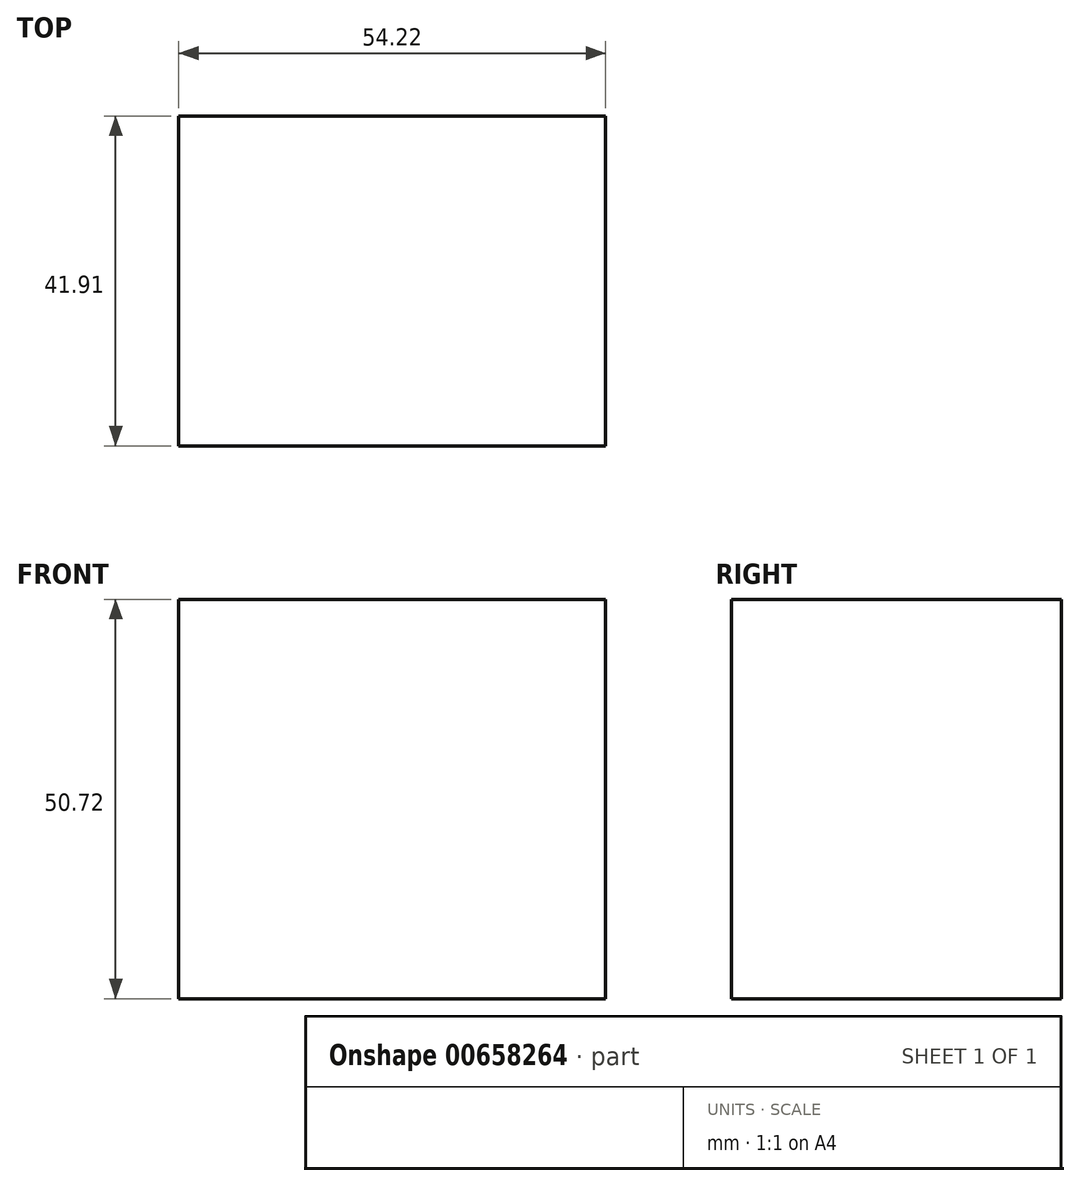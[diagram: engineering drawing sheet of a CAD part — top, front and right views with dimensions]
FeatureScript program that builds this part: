
annotation { "Feature Type Name" : "Feature", "Feature Type Description" : "" }
export const myFeature = defineFeature(function(context is Context, id is Id, definition is map)
    precondition{}
    {
        {
            var Q0;
            Q0=qCreatedBy(makeId("Front.planeOp"),FACE);
            var sketch = newSketch(context, id + "F0", { "sketchPlane" : qUnion([Q0])});
            skLineSegment(sketch, "E0.bottom", {"start": v(-67.21, 50.72) * mm, "end": v(-12.99, 50.72) * mm});
            skLineSegment(sketch, "E0.top", {"start": v(-67.21, 0) * mm, "end": v(-12.99, 0) * mm});
            skLineSegment(sketch, "E0.left", {"start": v(-67.21, 50.72) * mm, "end": v(-67.21, 0) * mm});
            skLineSegment(sketch, "E0.right", {"start": v(-12.99, 50.72) * mm, "end": v(-12.99, 0) * mm});
            skSolve(sketch);
        }
        {
            var Q0;
            Q0=makeQuery(id+"F0.imprint","IMPRINT",FACE,{"disambiguationData":[TD([[makeQuery(id+"F0.imprint","IMPRINT",EDGE,{"derivedFrom":sQuery(id+"F0.wireOp",EDGE,"E0.bottom")}),-1.0]])]});
            extrude(context, id + "F1", {"entities" : qUnion([Q0]), "depth" : 41.9 * mm, "offsetDistance" : 25.4 * mm});
        }
    });
